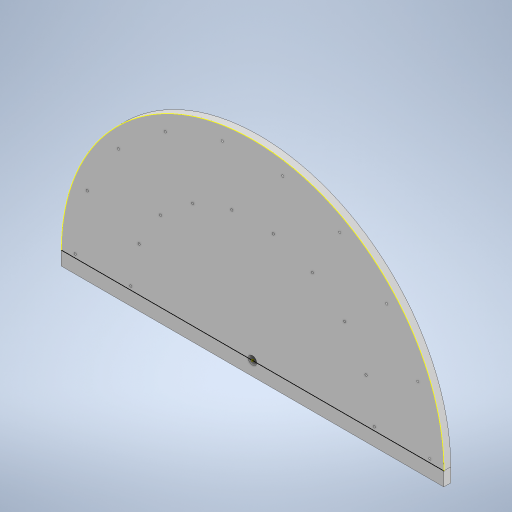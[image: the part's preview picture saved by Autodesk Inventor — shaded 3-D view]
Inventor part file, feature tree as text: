
AUTODESK INVENTOR PART (.ipt)
format: ipt  version: 2023 (Build 270158000, 158)  size: 333,312 bytes
history: native  units: mm
features: sketch x11, extrude x10
ambient origin geometry x8: Origin, YZ Plane, XZ Plane, XY Plane, X Axis, Y Axis, Z Axis, Center Point
bodies: Solide1 (feature_tree)
feature tree (21):
  extrude  "Extrusion1"  Depth=310.0mm
  sketch  "Esquisse2"
  extrude  "Extrusion2"  Depth=550.0mm
  extrude  "Extrusion3"  Depth=180.0mm
  extrude  "Extrusion4"  Depth=10.0mm TaperAngle=0.0deg
  extrude  "Extrusion6"  Depth=179.985088mm
  extrude  "Extrusion7"  Depth=5.0mm
  extrude  "Extrusion8"  [1 undecoded]
  extrude  "Extrusion9"  Depth=3.0mm
  extrude  "Extrusion10"  Depth=175.0mm
  extrude  "Extrusion11"  Depth=5.0mm
  sketch  "Esquisse1"
  sketch  "Esquisse3"
  sketch  "Esquisse4"
  sketch  "Esquisse5"
  sketch  "Esquisse6"
  sketch  "Esquisse7"
  sketch  "Esquisse8"
  sketch  "Esquisse9"
  sketch  "Esquisse11"
  sketch  "Esquisse12"
note: 1 required parameter value undecoded (feature->parameter linkage not recoverable at this tier; creation-order binding heuristic only, values carry confidence <= 0.55)
